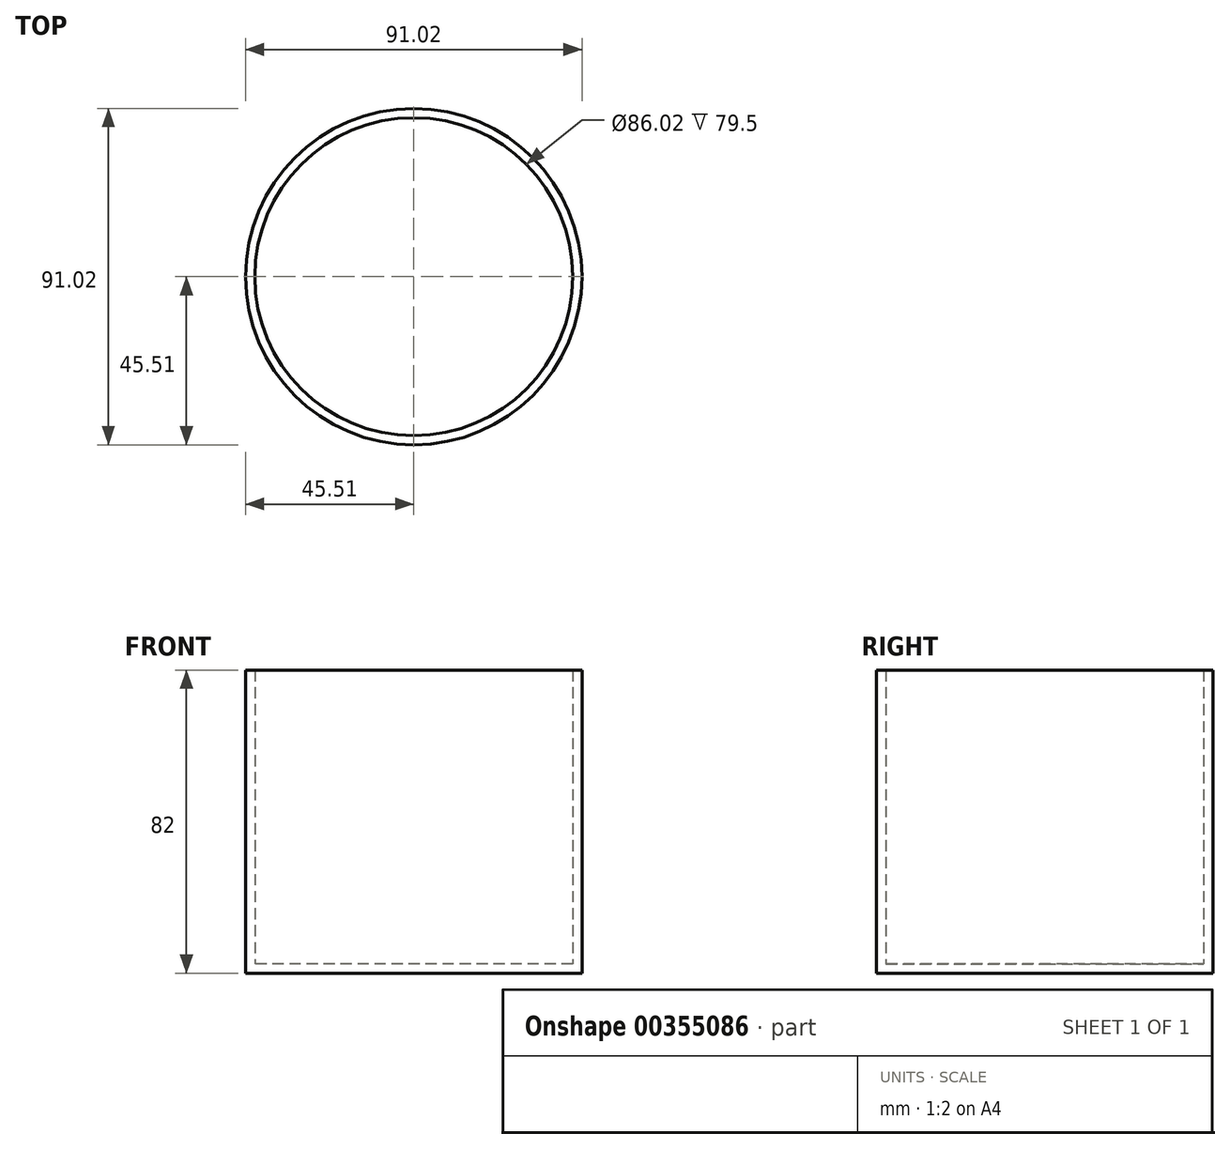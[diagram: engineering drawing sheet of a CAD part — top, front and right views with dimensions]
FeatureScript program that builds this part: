
annotation { "Feature Type Name" : "Feature", "Feature Type Description" : "" }
export const myFeature = defineFeature(function(context is Context, id is Id, definition is map)
    precondition{}
    {
        {
            var Q0;
            Q0=qCreatedBy(makeId("Top.planeOp"),FACE);
            var sketch = newSketch(context, id + "F0", { "sketchPlane" : qUnion([Q0])});
            skCircle(sketch, "E0", {"center": v(0, 0) * mm, "radius": 45.5 * mm});
            skSolve(sketch);
        }
        {
            var Q0;
            Q0 = qSketchRegion(id + "F0", true);
            extrude(context, id + "F1", {"entities" : qUnion([Q0]), "depth" : 82 * mm});
        }
        {
            var Q0;
            Q0=makeQuery(id+"F1.opExtrude","CAP_FACE",FACE,{"disambiguationData":[OSD([sQuery(id+"F0.wireOp",EDGE,"E0")])],"isStart":false});
            shell(context, id + "F2", {"entities" : qUnion([Q0]), "thickness" : 2.5 * mm});
        }
        {
            var Q0;
            Q0=qCreatedBy(makeId("Right.planeOp"),FACE);
            cPlane(context, id + "F3", {"entities" : qUnion([Q0]), "cplaneType" : CPlaneType.OFFSET, "offset" : 44 * mm, "width" : 150 * mm, "height" : 150 * mm});
        }
    });
